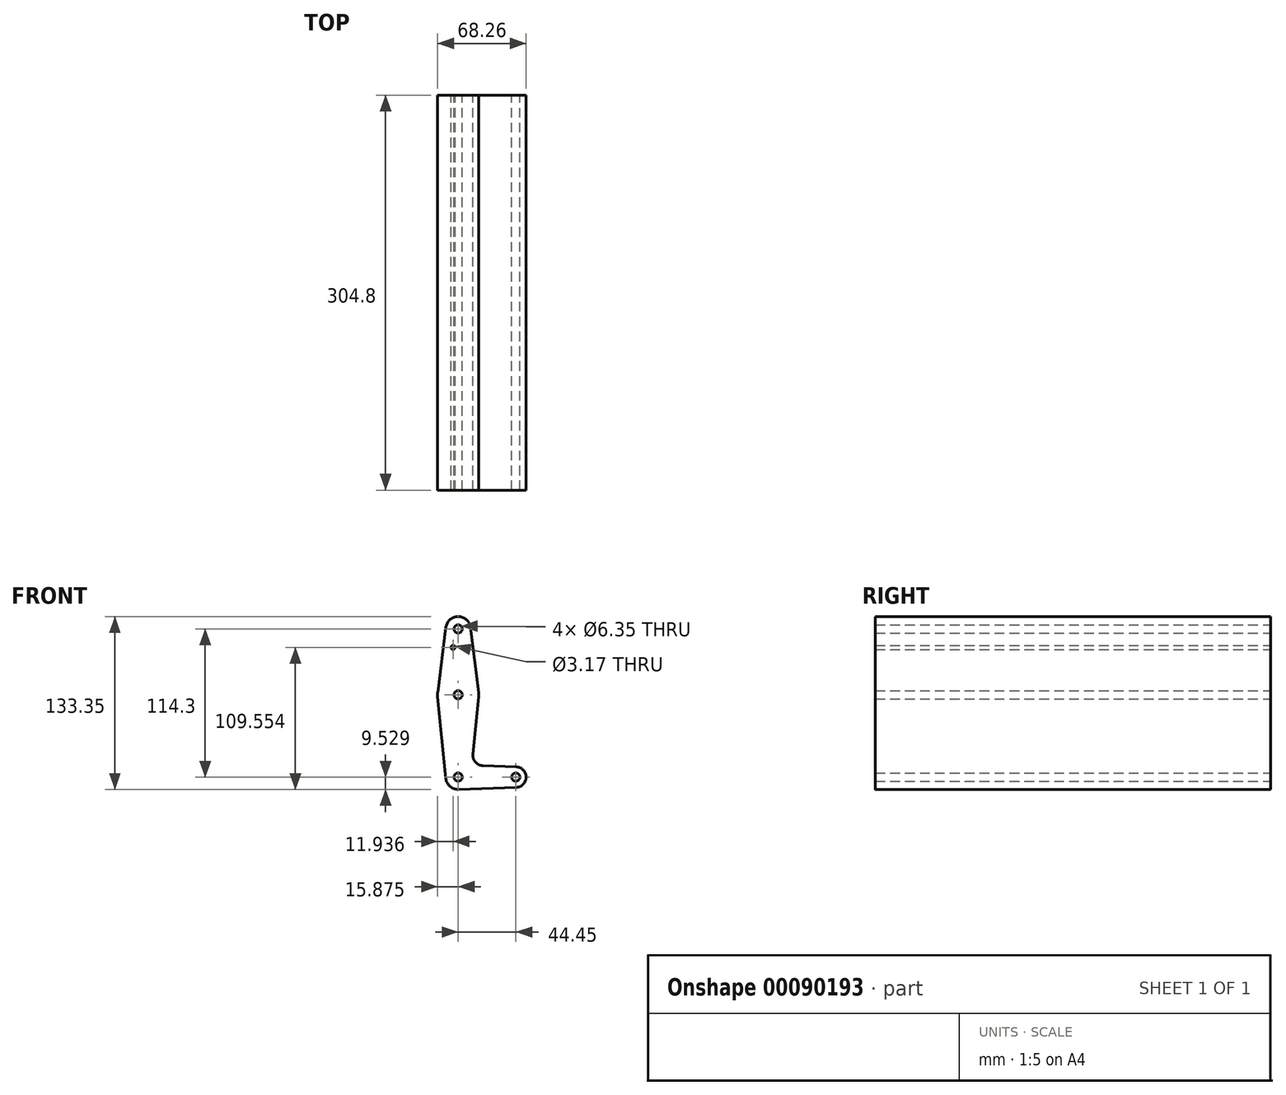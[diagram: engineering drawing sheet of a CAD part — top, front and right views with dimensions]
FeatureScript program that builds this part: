
annotation { "Feature Type Name" : "Feature", "Feature Type Description" : "" }
export const myFeature = defineFeature(function(context is Context, id is Id, definition is map)
    precondition{}
    {
        {
            var Q0;
            Q0=qCreatedBy(makeId("Front.planeOp"),FACE);
            var sketch = newSketch(context, id + "F0", { "sketchPlane" : qUnion([Q0])});
            skLineSegment(sketch, "E0", {"start": v(-41.6, 57.14) * mm, "end": v(-41.6, -57.16) * mm, "construction": true});
            skLineSegment(sketch, "E1", {"start": v(-41.6, -57.16) * mm, "end": v(2.84, -57.16) * mm, "construction": true});
            skCircle(sketch, "E2", {"center": v(-41.6, 57.14) * mm, "radius": 9.53 * mm});
            skCircle(sketch, "E3", {"center": v(-41.6, 6.34) * mm, "radius": 15.88 * mm});
            skCircle(sketch, "E4", {"center": v(-41.6, -57.16) * mm, "radius": 9.53 * mm});
            skCircle(sketch, "E5", {"center": v(2.84, -57.16) * mm, "radius": 7.94 * mm});
            skLineSegment(sketch, "E6", {"start": v(-51.06, 58.33) * mm, "end": v(-57.36, 8.32) * mm});
            skLineSegment(sketch, "E7", {"start": v(-57.4, 4.75) * mm, "end": v(-51.08, -58.11) * mm});
            skLineSegment(sketch, "E8", {"start": v(-25.8, 4.75) * mm, "end": v(-30.26, -39.57) * mm});
            skLineSegment(sketch, "E9", {"start": v(-41.26, -66.68) * mm, "end": v(3.13, -65.1) * mm});
            skLineSegment(sketch, "E10", {"start": v(-32.15, 58.33) * mm, "end": v(-25.85, 8.32) * mm});
            skLineSegment(sketch, "E11", {"start": v(-22.64, -48.31) * mm, "end": v(3.13, -49.23) * mm});
            skCircle(sketch, "E12", {"center": v(-41.6, 57.14) * mm, "radius": 3.18 * mm});
            skCircle(sketch, "E13", {"center": v(-41.6, 6.34) * mm, "radius": 3.18 * mm});
            skCircle(sketch, "E14", {"center": v(2.84, -57.16) * mm, "radius": 3.18 * mm});
            skCircle(sketch, "E15", {"center": v(-41.6, -57.16) * mm, "radius": 3.18 * mm});
            skCircle(sketch, "E16", {"center": v(-45.54, 42.86) * mm, "radius": 1.59 * mm});
            skArc(sketch, "E17.filletArc", {"start": v(-30.26, -39.57) * mm, "mid": v(-28.34, -45.6) * mm, "end": v(-22.64, -48.31) * mm});
            skSolve(sketch);
        }
        {
            var Q0;
            Q0 = qSketchRegion(id + "F0", true);
            extrude(context, id + "F1", {"entities" : qUnion([Q0]), "depth" : 304.8 * mm});
        }
    });
